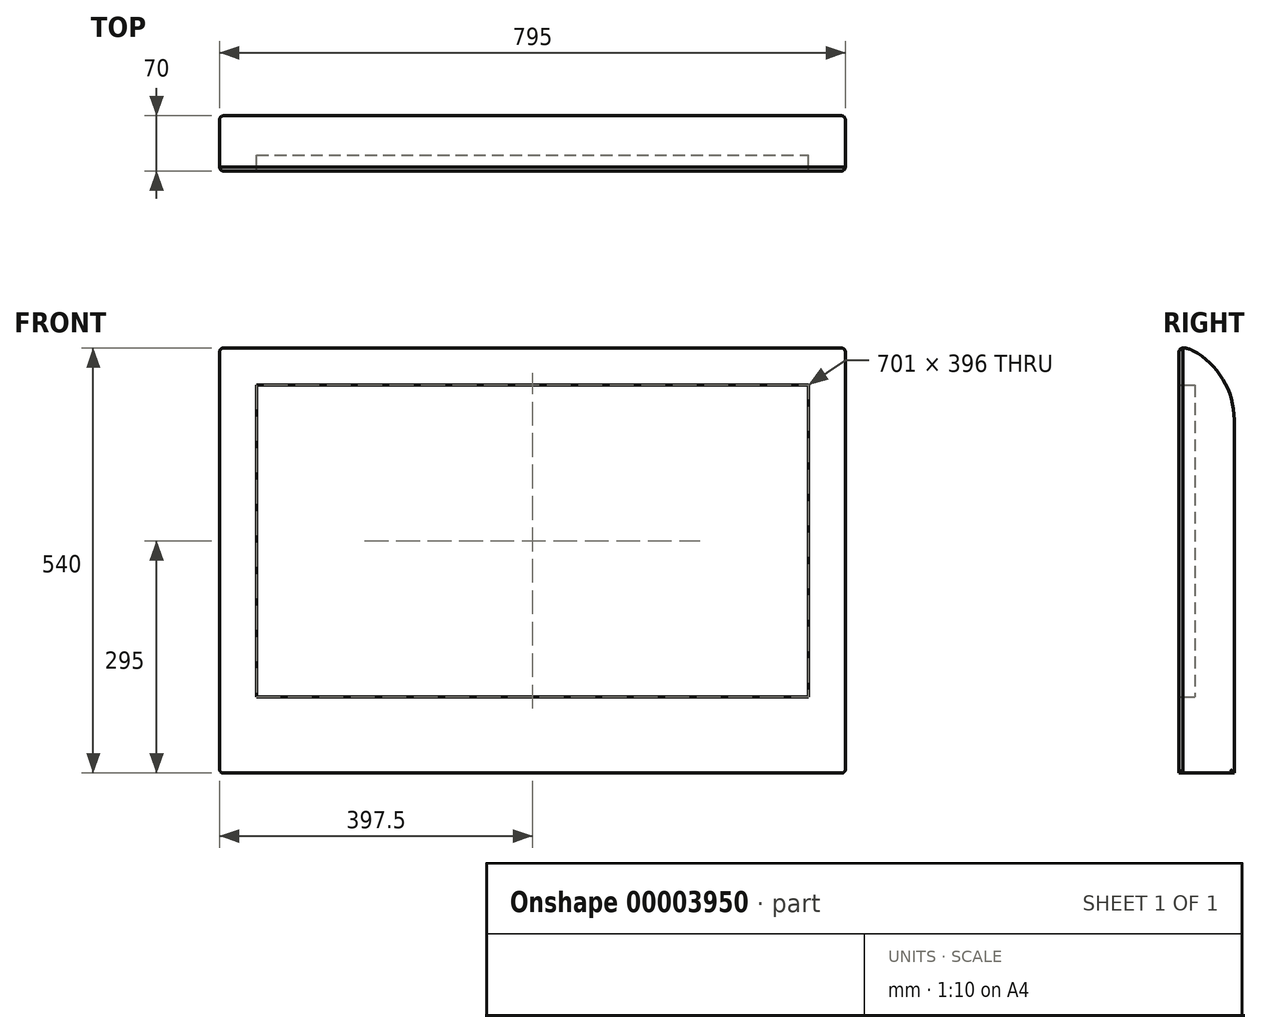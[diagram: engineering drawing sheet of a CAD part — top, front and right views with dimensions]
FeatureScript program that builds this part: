
annotation { "Feature Type Name" : "Feature", "Feature Type Description" : "" }
export const myFeature = defineFeature(function(context is Context, id is Id, definition is map)
    precondition{}
    {
        {
            var Q0;
            Q0=qCreatedBy(makeId("Front.planeOp"),FACE);
            var sketch = newSketch(context, id + "F0", { "sketchPlane" : qUnion([Q0])});
            skLineSegment(sketch, "E0.bottom", {"start": v(0, 0) * mm, "end": v(701, 0) * mm});
            skLineSegment(sketch, "E0.top", {"start": v(0, -396) * mm, "end": v(701, -396) * mm});
            skLineSegment(sketch, "E0.left", {"start": v(0, 0) * mm, "end": v(0, -396) * mm});
            skLineSegment(sketch, "E0.right", {"start": v(701, 0) * mm, "end": v(701, -396) * mm});
            skSolve(sketch);
        }
        {
            var Q0;
            Q0=makeQuery(id+"F0.imprint","IMPRINT",FACE,{"disambiguationData":[TD([[makeQuery(id+"F0.imprint","IMPRINT",EDGE,{"derivedFrom":sQuery(id+"F0.wireOp",EDGE,"E0.bottom")}),-1.0]])]});
            extrude(context, id + "F1", {"entities" : qUnion([Q0]), "depth" : 15 * mm});
        }
        {
            var Q0;
            Q0=makeQuery(id+"F1.opExtrude","CAP_FACE",FACE,{"disambiguationData":[OSD([sQuery(id+"F0.wireOp",EDGE,"E0.bottom"),sQuery(id+"F0.wireOp",EDGE,"E0.top"),sQuery(id+"F0.wireOp",EDGE,"E0.left"),sQuery(id+"F0.wireOp",EDGE,"E0.right")])],"isStart":false});
            var sketch = newSketch(context, id + "F2", { "sketchPlane" : qUnion([Q0])});
            skLineSegment(sketch, "E1.bottom", {"start": v(0, 0) * mm, "end": v(701, 0) * mm});
            skLineSegment(sketch, "E1.top", {"start": v(0, -396) * mm, "end": v(701, -396) * mm});
            skLineSegment(sketch, "E1.left", {"start": v(0, 0) * mm, "end": v(0, -396) * mm});
            skLineSegment(sketch, "E1.right", {"start": v(701, 0) * mm, "end": v(701, -396) * mm});
            skLineSegment(sketch, "E2.bottom", {"start": v(-47, 47) * mm, "end": v(748, 47) * mm});
            skLineSegment(sketch, "E2.top", {"start": v(-47, -493) * mm, "end": v(748, -493) * mm});
            skLineSegment(sketch, "E2.left", {"start": v(-47, 47) * mm, "end": v(-47, -493) * mm});
            skLineSegment(sketch, "E2.right", {"start": v(748, 47) * mm, "end": v(748, -493) * mm});
            skSolve(sketch);
        }
        {
            var Q0;
            Q0=makeQuery(id+"F2.imprint","IMPRINT",FACE,{"disambiguationData":[TD([[makeQuery(id+"F2.imprint","IMPRINT",EDGE,{"derivedFrom":sQuery(id+"F2.wireOp",EDGE,"E1.bottom")}),1.0]])]});
            extrude(context, id + "F3", {"entities" : qUnion([Q0]), "depth" : 5 * mm});
        }
        {
            var Q0;
            Q0=makeQuery(id+"F3.opExtrude","SWEPT_FACE",FACE,{"disambiguationData":[OSD([sQuery(id+"F2.wireOp",EDGE,"E2.left")])]});
            var sketch = newSketch(context, id + "F4", { "sketchPlane" : qUnion([Q0])});
            skLineSegment(sketch, "E3", {"start": v(15, -493) * mm, "end": v(-50, -493) * mm});
            skLineSegment(sketch, "E4", {"start": v(-50, -493) * mm, "end": v(-50, -44.23) * mm});
            skArc(sketch, "E5", {"start": v(15, 47) * mm, "mid": v(8.74, 46.23) * mm, "end": v(2.85, 43.95) * mm});
            skArc(sketch, "E6", {"start": v(2.85, 43.95) * mm, "mid": v(-35.78, 7.17) * mm, "end": v(-50, -44.23) * mm});
            skLineSegment(sketch, "E7", {"start": v(15, 47) * mm, "end": v(15, -493) * mm});
            skSolve(sketch);
        }
        {
            var Q0;
            Q0=makeQuery(id+"F4.imprint","IMPRINT",FACE,{"disambiguationData":[TD([[makeQuery(id+"F4.imprint","IMPRINT",EDGE,{"derivedFrom":sQuery(id+"F4.wireOp",EDGE,"E3")}),-1.0]])]});
            extrude(context, id + "F5", {"entities" : qUnion([Q0]), "oppositeDirection" : true, "depth" : (701 + 47 + 47) * mm});
        }
        {
            var Q0;
            Q0=makeQuery(id+"F5.opExtrude","CAP_EDGE",EDGE,{"disambiguationData":[OSD([sQuery(id+"F4.wireOp",EDGE,"E5")])],"isStart":true});
            var Q1;
            Q1=makeQuery(id+"F3.opExtrude","SWEPT_EDGE",EDGE,{"disambiguationData":[OSD([sQuery(id+"F2.wireOp",EDGE,"E2.bottom"),sQuery(id+"F2.wireOp",EDGE,"E2.left")])]});
            var Q2;
            Q2=makeQuery(id+"F5.opExtrude","CAP_EDGE",EDGE,{"disambiguationData":[OSD([sQuery(id+"F4.wireOp",EDGE,"E3")])],"isStart":true});
            var Q3;
            Q3=makeQuery(id+"F3.opExtrude","SWEPT_EDGE",EDGE,{"disambiguationData":[OSD([sQuery(id+"F2.wireOp",EDGE,"E2.top"),sQuery(id+"F2.wireOp",EDGE,"E2.left")])]});
            var Q4;
            Q4=makeQuery(id+"F3.opExtrude","SWEPT_EDGE",EDGE,{"disambiguationData":[OSD([sQuery(id+"F2.wireOp",EDGE,"E2.bottom"),sQuery(id+"F2.wireOp",EDGE,"E2.right")])]});
            var Q5;
            Q5=makeQuery(id+"F5.opExtrude","CAP_EDGE",EDGE,{"disambiguationData":[OSD([sQuery(id+"F4.wireOp",EDGE,"E5")])],"isStart":false});
            var Q6;
            Q6=makeQuery(id+"F3.opExtrude","CAP_EDGE",EDGE,{"disambiguationData":[OSD([sQuery(id+"F2.wireOp",EDGE,"E2.bottom")])],"isStart":false});
            var Q7;
            Q7=makeQuery(id+"F5.opExtrude","CAP_EDGE",EDGE,{"disambiguationData":[OSD([sQuery(id+"F4.wireOp",EDGE,"E3")])],"isStart":false});
            var Q8;
            Q8=makeQuery(id+"F3.opExtrude","SWEPT_EDGE",EDGE,{"disambiguationData":[OSD([sQuery(id+"F2.wireOp",EDGE,"E2.top"),sQuery(id+"F2.wireOp",EDGE,"E2.right")])]});
            var Q9;
            Q9=makeQuery(id+"F5.opExtrude","CAP_EDGE",EDGE,{"disambiguationData":[OSD([sQuery(id+"F4.wireOp",EDGE,"E6")])],"isStart":false});
            var Q10;
            Q10=makeQuery(id+"F3.opExtrude","CAP_EDGE",EDGE,{"disambiguationData":[OSD([sQuery(id+"F2.wireOp",EDGE,"E2.right")])],"isStart":false});
            var Q11;
            Q11=makeQuery(id+"F3.opExtrude","CAP_EDGE",EDGE,{"disambiguationData":[OSD([sQuery(id+"F2.wireOp",EDGE,"E2.left")])],"isStart":false});
            fillet(context, id + "F6", {"entities" : qUnion([Q0, Q1, Q2, Q3, Q4, Q5, Q6, Q7, Q8, Q9, Q10, Q11]), "radius" : 5 * mm, "tangentPropagation" : true, "allowEdgeOverflow" : false});
        }
    });
